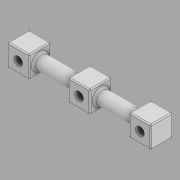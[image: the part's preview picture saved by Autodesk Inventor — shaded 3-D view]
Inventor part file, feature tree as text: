
AUTODESK INVENTOR PART (.ipt)
format: ipt  version: 2020 (Build 240168000, 168)  size: 202,752 bytes
history: native  units: mm
features: extrude x5, sketch x5, fillet x2, other x1
ambient origin geometry x8: Origin, YZ Plane, XZ Plane, XY Plane, X Axis, Y Axis, Z Axis, Center Point
bodies: Body1 (feature_tree)
feature tree (13):
  other  "Sólido1"
  extrude  "Extrusión1"  Depth=10.0mm
  extrude  "Extrusión2"  Depth=10.0mm TaperAngle=0.0deg
  extrude  "Extrusión3"  Depth=18.0mm TaperAngle=0.0deg
  extrude  "Extrusión4"  Depth=10.0mm
  extrude  "Extrusión5"  Depth=4.0mm
  fillet  "Empalme1"  Radius=10.0mm
  fillet  "Empalme2"  Radius=6.0mm
  sketch  "Boceto1"  dims[d0=10.0mm d1=10.0mm]
  sketch  "Boceto2"  dims[d2=4.0mm d3=10.0mm d4=0.0mm]
  sketch  "Boceto3"  dims[d5=6.0mm d6=18.0mm d7=0.0mm]
  sketch  "Boceto4"  dims[d8=10.0mm d9=10.0mm]
  sketch  "Boceto5"  dims[d10=28.0mm d11=4.0mm d12=10.0mm d13=0.0mm d14=6.0mm d15=18.0mm d16=0.0mm d17=10.0mm d18=10.0mm d19=28.0mm d20=4.0mm d21=10.0mm d22=0.0mm d23=1.0mm d24=0.5mm]
